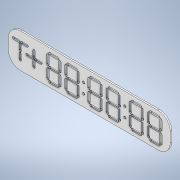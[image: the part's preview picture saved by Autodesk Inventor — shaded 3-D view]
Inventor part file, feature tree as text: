
AUTODESK INVENTOR PART (.ipt)
format: ipt  version: 2021 (Build 250183000, 183)  size: 1,112,576 bytes
history: native  units: in
note: dims shown in document units (in); Inventor stores cm internally (conversion verified against a paired STEP export)
features: other x37, extrude x2, sketch x1
ambient origin geometry x8: Origin, YZ Plane, XZ Plane, XY Plane, X Axis, Y Axis, Z Axis, Center Point
bodies: Solid1 (feature_tree)
feature tree (40):
  other  "Blocks"
  extrude  "Extrusion1"  TaperAngle=135.0deg  [1 undecoded]
  extrude  "Extrusion3"  Depth=0.8661in
  other  "Single Segment"
  other  "7 Segment Digit"
  other  "Slanted Segment Large"
  other  "+ sign"
  other  "Dot"
  other  "Clock Face with T +-"
  other  "Clock Front Face Outline"
  other  "Small Segmemt"
  sketch  "Sketch5"  dims[d10=62.9921in d11=78.7402in d29=0.1181in d30=0.0in d105=0.0866in d108=0.0866in d111=0.0866in d112=0.0866in d113=0.0866in d114=0.0866in d115=0.0866in d116=0.0394in d117=0.1969in d121=0.0866in d122=0.0866in d126=135.0deg d127=0.8661in d128=135.0deg d129=0.0984in d131=0.0433in d132=0.0433in d137=0.0433in d138=0.0433in d139=0.0433in d140=0.0433in d141=0.0433in d142=0.0433in d143=0.0433in d144=0.0433in d145=0.0433in d146=0.0433in d150=0.0433in d151=0.0433in d152=0.0433in d153=0.0433in d294=0.126in d295=0.126in d296=0.315in d297=0.126in d298=0.126in d299=2.2441in d304=0.126in d305=0.126in d306=0.126in d307=0.126in d311=0.0787in d312=0.0787in d314=0.0787in d315=0.0787in d316=0.0787in d317=0.0787in d318=0.0787in d319=0.0787in d320=0.0394in d321=0.0394in d322=0.0394in d323=0.0394in d348=0.1969in d349=0.8661in d350=0.0866in d352=0.0118in d353=0.0118in d358=0.0118in d359=0.0118in d360=0.1969in d361=0.1969in d362=0.2953in d363=0.6693in d364=0.2953in d365=0.6693in d366=0.2953in d367=0.0in d368=0.0in d369=0.0in d370=0.0in d371=0.0in d372=0.5906in d373=0.0in d374=0.6299in d375=0.2362in d376=0.2362in d377=0.5354in d378=0.6299in d379=0.2362in d380=0.5906in d381=0.0in d402=1.9528in d429=12.9921in d430=2.7559in d431=0.9843in d462=0.0866in d463=0.0866in d464=0.0866in d465=0.0866in d466=0.0866in d467=0.0866in d468=0.0866in d469=0.0394in d470=0.1969in d471=0.0866in d472=0.0866in d473=135.0deg d474=0.6299in d475=135.0deg d476=0.0984in d477=0.1969in d478=0.6299in d479=0.0866in d480=0.0118in d481=0.0118in d482=0.0118in d483=0.0118in d496=0.0787in d497=0.0787in d501=0.0394in d502=0.0394in d503=0.0in d504=0.0in d505=0.039in d506=0.039in d507=0.039in d508=0.039in d509=0.9055in d510=0.9843in d511=0.9685in d514=0.0197in d515=0.0394in d516=0.0394in d517=0.0394in d518=0.0in d519=0.039in d520=0.4331in d522=0.9055in d523=0.0in d524=0.0591in d525=0.315in d526=0.2913in d527=0.8661in d528=0.6575in d529=0.315in d530=0.1181in d531=0.0in]
  other  "Single Segment:9"
  other  "Single Segment:10"
  other  "Single Segment:11"
  other  "Single Segment:12"
  other  "Single Segment:13"
  other  "Single Segment:14"
  other  "Single Segment:15"
  other  "7 Segment Digit:8"
  other  "7 Segment Digit:9"
  other  "7 Segment Digit:10"
  other  "7 Segment Digit:11"
  other  "7 Segment Digit:12"
  other  "7 Segment Digit:13"
  other  "Dot:7"
  other  "Dot:8"
  other  "Dot:9"
  other  "Dot:10"
  other  "Clock Front Face Outline:1"
  other  "Small Segmemt:1"
  other  "Small Segmemt:2"
  other  "Small Segmemt:3"
  other  "Small Segmemt:4"
  other  "+ sign:1"
  other  "Small Segmemt:5"
  other  "Small Segmemt:6"
  other  "Small Segmemt:7"
  other  "Small Segmemt:8"
  other  "Clock Face with T +-:1"
note: 1 required parameter value undecoded (feature->parameter linkage not recoverable at this tier; creation-order binding heuristic only, values carry confidence <= 0.55)
